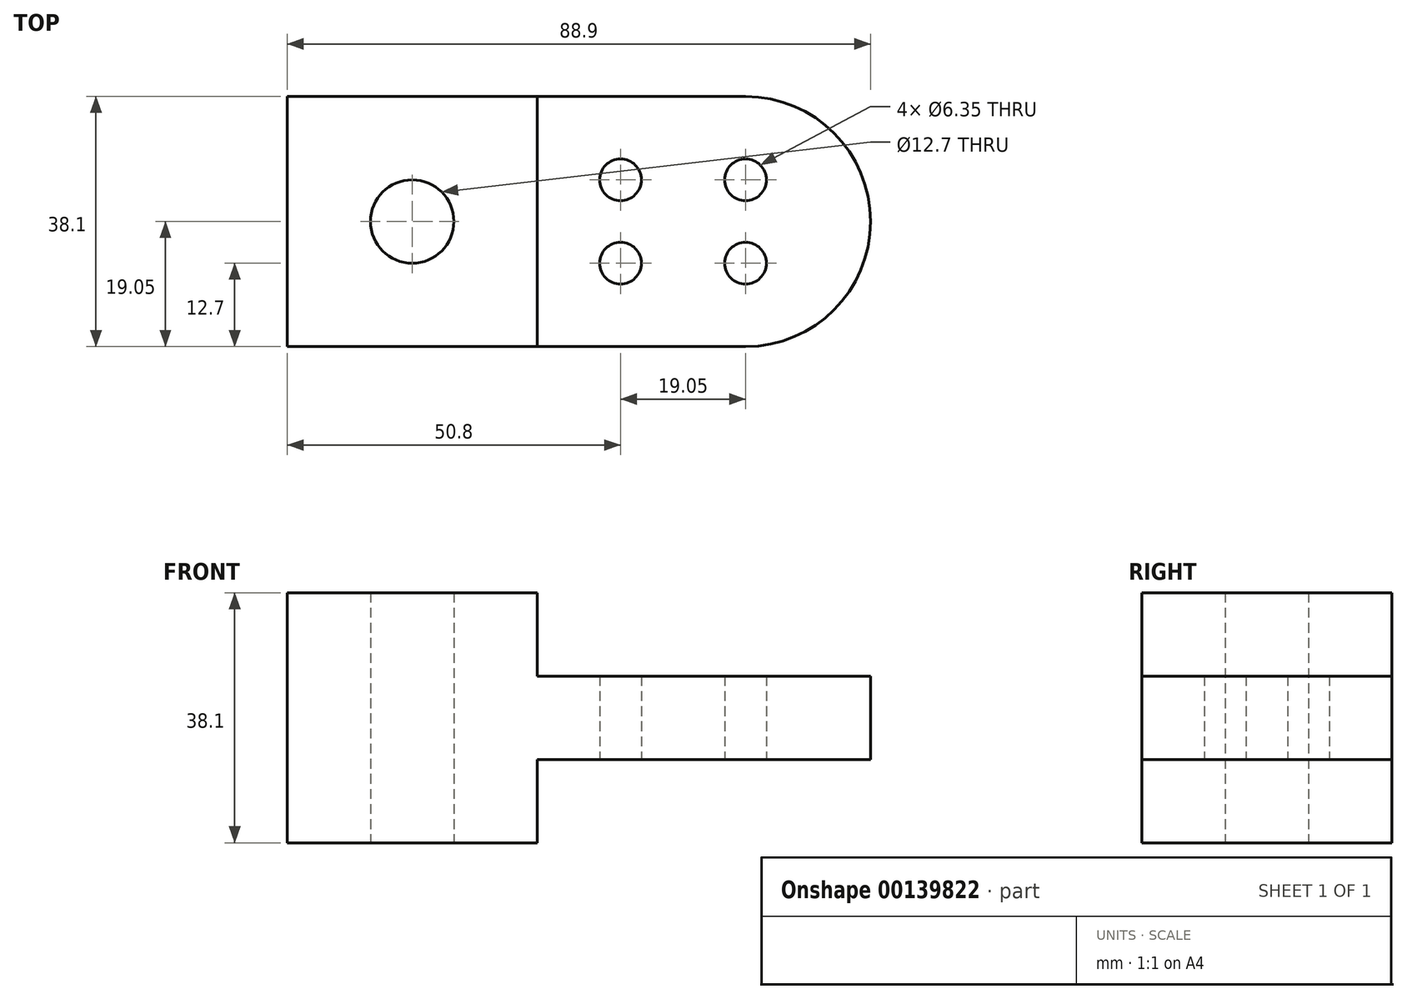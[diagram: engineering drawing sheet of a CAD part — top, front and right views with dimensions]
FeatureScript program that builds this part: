
annotation { "Feature Type Name" : "Feature", "Feature Type Description" : "" }
export const myFeature = defineFeature(function(context is Context, id is Id, definition is map)
    precondition{}
    {
        {
            var Q0;
            Q0=qCreatedBy(makeId("Top.planeOp"),FACE);
            var sketch = newSketch(context, id + "F0", { "sketchPlane" : qUnion([Q0])});
            skLineSegment(sketch, "E0", {"start": v(0, 0) * mm, "end": v(0, 38.1) * mm});
            skLineSegment(sketch, "E1", {"start": v(0, 38.1) * mm, "end": v(38.1, 38.1) * mm});
            skLineSegment(sketch, "E2", {"start": v(0, 0) * mm, "end": v(38.1, 0) * mm});
            skLineSegment(sketch, "E3", {"start": v(38.1, 38.1) * mm, "end": v(38.1, 0) * mm});
            skLineSegment(sketch, "E4", {"start": v(38.1, 38.1) * mm, "end": v(69.85, 38.1) * mm});
            skLineSegment(sketch, "E5", {"start": v(38.1, 0) * mm, "end": v(69.85, 0) * mm});
            skArc(sketch, "E6", {"start": v(69.85, 0) * mm, "mid": v(88.9, 19.05) * mm, "end": v(69.85, 38.1) * mm});
            skCircle(sketch, "E7", {"center": v(19.05, 19.05) * mm, "radius": 6.35 * mm});
            skCircle(sketch, "E8", {"center": v(50.8, 25.4) * mm, "radius": 3.18 * mm});
            skCircle(sketch, "E9", {"center": v(50.8, 12.7) * mm, "radius": 3.18 * mm});
            skCircle(sketch, "E10", {"center": v(69.85, 25.4) * mm, "radius": 3.18 * mm});
            skCircle(sketch, "E11", {"center": v(69.85, 12.7) * mm, "radius": 3.18 * mm});
            skSolve(sketch);
        }
        {
            var Q0;
            Q0=makeQuery(id+"F0.imprint","IMPRINT",FACE,{"disambiguationData":[TD([[makeQuery(id+"F0.imprint","IMPRINT",EDGE,{"derivedFrom":sQuery(id+"F0.wireOp",EDGE,"E0")}),-1.0]])]});
            extrude(context, id + "F1", {"entities" : qUnion([Q0]), "endBound" : BoundingType.SYMMETRIC, "depth" : 38.1 * mm});
        }
        {
            var Q0;
            Q0=makeQuery(id+"F0.imprint","IMPRINT",FACE,{"disambiguationData":[TD([[makeQuery(id+"F0.imprint","IMPRINT",EDGE,{"derivedFrom":sQuery(id+"F0.wireOp",EDGE,"E3")}),1.0]])]});
            extrude(context, id + "F2", {"entities" : qUnion([Q0]), "operationType" : NewBodyOperationType.ADD, "endBound" : BoundingType.SYMMETRIC, "depth" : 12.7 * mm});
        }
    });
